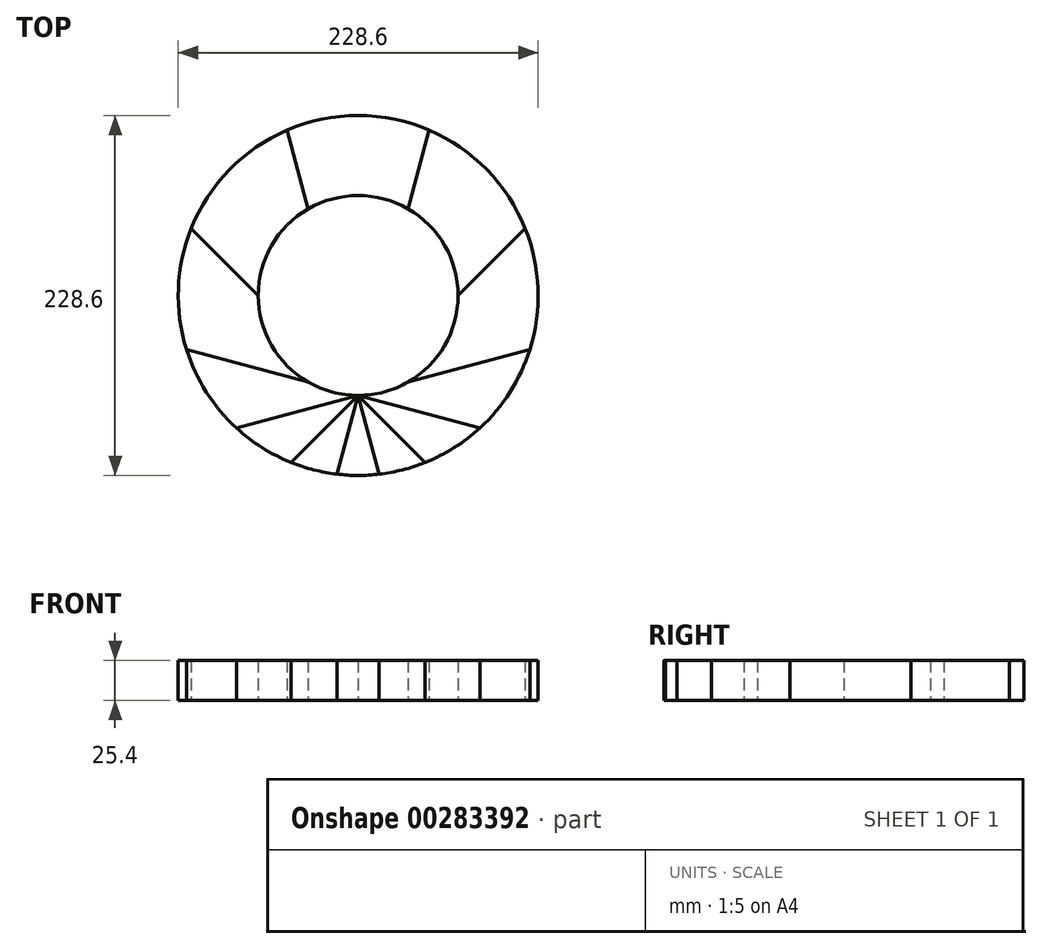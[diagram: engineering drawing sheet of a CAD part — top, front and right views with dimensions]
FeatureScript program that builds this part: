
annotation { "Feature Type Name" : "Feature", "Feature Type Description" : "" }
export const myFeature = defineFeature(function(context is Context, id is Id, definition is map)
    precondition{}
    {
        {
            var Q0;
            Q0=qCreatedBy(makeId("Top.planeOp"),FACE);
            var sketch = newSketch(context, id + "F0", { "sketchPlane" : qUnion([Q0])});
            skCircle(sketch, "E0", {"center": v(0, 0) * mm, "radius": 114.3 * mm});
            skLineSegment(sketch, "E1", {"start": v(0, 0) * mm, "end": v(0, -63.5) * mm, "construction": true});
            skCircle(sketch, "E2", {"center": v(0, 0) * mm, "radius": 63.5 * mm});
            skCircle(sketch, "E3.cCircle", {"center": v(0, -63.5) * mm, "radius": 177.8 * mm, "construction": true});
            skLineSegment(sketch, "E3.0", {"start": v(-47.64, 114.3) * mm, "end": v(47.64, 114.3) * mm, "construction": true});
            skLineSegment(sketch, "E3.1", {"start": v(47.64, 114.3) * mm, "end": v(130.16, 66.66) * mm, "construction": true});
            skLineSegment(sketch, "E3.2", {"start": v(130.16, 66.66) * mm, "end": v(177.8, -15.86) * mm, "construction": true});
            skLineSegment(sketch, "E3.3", {"start": v(177.8, -15.86) * mm, "end": v(177.8, -111.14) * mm, "construction": true});
            skLineSegment(sketch, "E3.4", {"start": v(177.8, -111.14) * mm, "end": v(130.16, -193.66) * mm, "construction": true});
            skLineSegment(sketch, "E3.5", {"start": v(130.16, -193.66) * mm, "end": v(47.64, -241.3) * mm, "construction": true});
            skLineSegment(sketch, "E3.6", {"start": v(47.64, -241.3) * mm, "end": v(-47.64, -241.3) * mm, "construction": true});
            skLineSegment(sketch, "E3.7", {"start": v(-47.64, -241.3) * mm, "end": v(-130.16, -193.66) * mm, "construction": true});
            skLineSegment(sketch, "E3.8", {"start": v(-130.16, -193.66) * mm, "end": v(-177.8, -111.14) * mm, "construction": true});
            skLineSegment(sketch, "E3.9", {"start": v(-177.8, -111.14) * mm, "end": v(-177.8, -15.86) * mm, "construction": true});
            skLineSegment(sketch, "E3.10", {"start": v(-177.8, -15.86) * mm, "end": v(-130.16, 66.66) * mm, "construction": true});
            skLineSegment(sketch, "E3.11", {"start": v(-130.16, 66.66) * mm, "end": v(-47.64, 114.3) * mm, "construction": true});
            skPoint(sketch, "E3.0.midPoint", {"position": v(0, 114.3) * mm});
            skLineSegment(sketch, "E4", {"start": v(0, -63.5) * mm, "end": v(177.8, -111.14) * mm});
            skLineSegment(sketch, "E5.1.0", {"start": v(0, -63.5) * mm, "end": v(177.8, -15.86) * mm});
            skLineSegment(sketch, "E5.2.0", {"start": v(0, -63.5) * mm, "end": v(130.16, 66.66) * mm});
            skLineSegment(sketch, "E5.3.0", {"start": v(0, -63.5) * mm, "end": v(47.64, 114.3) * mm});
            skLineSegment(sketch, "E5.4.0", {"start": v(0, -63.5) * mm, "end": v(-47.64, 114.3) * mm});
            skLineSegment(sketch, "E5.5.0", {"start": v(0, -63.5) * mm, "end": v(-130.16, 66.66) * mm});
            skLineSegment(sketch, "E5.6.0", {"start": v(0, -63.5) * mm, "end": v(-177.8, -15.86) * mm});
            skLineSegment(sketch, "E5.7.0", {"start": v(0, -63.5) * mm, "end": v(-177.8, -111.14) * mm});
            skLineSegment(sketch, "E5.8.0", {"start": v(0, -63.5) * mm, "end": v(-130.16, -193.66) * mm});
            skLineSegment(sketch, "E5.9.0", {"start": v(0, -63.5) * mm, "end": v(-47.64, -241.3) * mm});
            skLineSegment(sketch, "E5.10.0", {"start": v(0, -63.5) * mm, "end": v(47.64, -241.3) * mm});
            skLineSegment(sketch, "E5.11.0", {"start": v(0, -63.5) * mm, "end": v(130.16, -193.66) * mm});
            skSolve(sketch);
        }
        {
            var Q0;
            {var subQ0=sQuery(id+"F0.wireOp",EDGE,"E5.5.0");var subQ1=sQuery(id+"F0.wireOp",EDGE,"E0");var subQ2=makeQuery(id+"F0.imprint","INTERSECT",VERTEX,{"derivedFrom":[subQ1,subQ0]});Q0=makeQuery(id+"F0.imprint","IMPRINT",FACE,{"disambiguationData":[TD([[makeQuery(id+"F0.imprint","IMPRINT",EDGE,{"disambiguationData":[TD([[subQ2,-1.0]])],"derivedFrom":subQ1}),1.0]])]});}
            var Q1;
            {var subQ0=sQuery(id+"F0.wireOp",EDGE,"E5.7.0");var subQ1=sQuery(id+"F0.wireOp",EDGE,"E0");var subQ2=makeQuery(id+"F0.imprint","INTERSECT",VERTEX,{"derivedFrom":[subQ1,subQ0]});Q1=makeQuery(id+"F0.imprint","IMPRINT",FACE,{"disambiguationData":[TD([[makeQuery(id+"F0.imprint","IMPRINT",EDGE,{"disambiguationData":[TD([[subQ2,-1.0]])],"derivedFrom":subQ1}),1.0]])]});}
            var Q2;
            {var subQ0=sQuery(id+"F0.wireOp",EDGE,"E5.9.0");var subQ1=sQuery(id+"F0.wireOp",EDGE,"E0");var subQ2=makeQuery(id+"F0.imprint","INTERSECT",VERTEX,{"derivedFrom":[subQ1,subQ0]});Q2=makeQuery(id+"F0.imprint","IMPRINT",FACE,{"disambiguationData":[TD([[makeQuery(id+"F0.imprint","IMPRINT",EDGE,{"disambiguationData":[TD([[subQ2,-1.0]])],"derivedFrom":subQ1}),1.0]])]});}
            var Q3;
            {var subQ0=sQuery(id+"F0.wireOp",EDGE,"E5.11.0");var subQ1=sQuery(id+"F0.wireOp",EDGE,"E0");var subQ2=makeQuery(id+"F0.imprint","INTERSECT",VERTEX,{"derivedFrom":[subQ1,subQ0]});Q3=makeQuery(id+"F0.imprint","IMPRINT",FACE,{"disambiguationData":[TD([[makeQuery(id+"F0.imprint","IMPRINT",EDGE,{"disambiguationData":[TD([[subQ2,-1.0]])],"derivedFrom":subQ1}),1.0]])]});}
            var Q4;
            {var subQ0=sQuery(id+"F0.wireOp",EDGE,"E5.2.0");var subQ1=sQuery(id+"F0.wireOp",EDGE,"E0");var subQ2=makeQuery(id+"F0.imprint","INTERSECT",VERTEX,{"derivedFrom":[subQ1,subQ0]});Q4=makeQuery(id+"F0.imprint","IMPRINT",FACE,{"disambiguationData":[TD([[makeQuery(id+"F0.imprint","IMPRINT",EDGE,{"disambiguationData":[TD([[subQ2,1.0]])],"derivedFrom":subQ1}),1.0]])]});}
            var Q5;
            {var subQ0=sQuery(id+"F0.wireOp",EDGE,"E5.3.0");var subQ1=sQuery(id+"F0.wireOp",EDGE,"E0");var subQ2=makeQuery(id+"F0.imprint","INTERSECT",VERTEX,{"derivedFrom":[subQ1,subQ0]});Q5=makeQuery(id+"F0.imprint","IMPRINT",FACE,{"disambiguationData":[TD([[makeQuery(id+"F0.imprint","IMPRINT",EDGE,{"disambiguationData":[TD([[subQ2,-1.0]])],"derivedFrom":subQ1}),1.0]])]});}
            extrude(context, id + "F1", {"entities" : qUnion([Q0, Q1, Q2, Q3, Q4, Q5]), "depth" : 25.4 * mm, "offsetDistance" : 25.4 * mm});
        }
        {
            var Q0;
            {var subQ0=sQuery(id+"F0.wireOp",EDGE,"E5.6.0");var subQ1=sQuery(id+"F0.wireOp",EDGE,"E0");var subQ2=makeQuery(id+"F0.imprint","INTERSECT",VERTEX,{"derivedFrom":[subQ1,subQ0]});Q0=makeQuery(id+"F0.imprint","IMPRINT",FACE,{"disambiguationData":[TD([[makeQuery(id+"F0.imprint","IMPRINT",EDGE,{"disambiguationData":[TD([[subQ2,-1.0]])],"derivedFrom":subQ1}),1.0]])]});}
            var Q1;
            {var subQ0=sQuery(id+"F0.wireOp",EDGE,"E5.4.0");var subQ1=sQuery(id+"F0.wireOp",EDGE,"E0");var subQ2=makeQuery(id+"F0.imprint","INTERSECT",VERTEX,{"derivedFrom":[subQ1,subQ0]});Q1=makeQuery(id+"F0.imprint","IMPRINT",FACE,{"disambiguationData":[TD([[makeQuery(id+"F0.imprint","IMPRINT",EDGE,{"disambiguationData":[TD([[subQ2,-1.0]])],"derivedFrom":subQ1}),1.0]])]});}
            var Q2;
            {var subQ0=sQuery(id+"F0.wireOp",EDGE,"E5.3.0");var subQ1=sQuery(id+"F0.wireOp",EDGE,"E0");var subQ2=makeQuery(id+"F0.imprint","INTERSECT",VERTEX,{"derivedFrom":[subQ1,subQ0]});Q2=makeQuery(id+"F0.imprint","IMPRINT",FACE,{"disambiguationData":[TD([[makeQuery(id+"F0.imprint","IMPRINT",EDGE,{"disambiguationData":[TD([[subQ2,1.0]])],"derivedFrom":subQ1}),1.0]])]});}
            var Q3;
            {var subQ0=sQuery(id+"F0.wireOp",EDGE,"E4");var subQ1=sQuery(id+"F0.wireOp",EDGE,"E0");var subQ2=makeQuery(id+"F0.imprint","INTERSECT",VERTEX,{"derivedFrom":[subQ1,subQ0]});Q3=makeQuery(id+"F0.imprint","IMPRINT",FACE,{"disambiguationData":[TD([[makeQuery(id+"F0.imprint","IMPRINT",EDGE,{"disambiguationData":[TD([[subQ2,-1.0]])],"derivedFrom":subQ1}),1.0]])]});}
            var Q4;
            {var subQ0=sQuery(id+"F0.wireOp",EDGE,"E5.10.0");var subQ1=sQuery(id+"F0.wireOp",EDGE,"E0");var subQ2=makeQuery(id+"F0.imprint","INTERSECT",VERTEX,{"derivedFrom":[subQ1,subQ0]});Q4=makeQuery(id+"F0.imprint","IMPRINT",FACE,{"disambiguationData":[TD([[makeQuery(id+"F0.imprint","IMPRINT",EDGE,{"disambiguationData":[TD([[subQ2,-1.0]])],"derivedFrom":subQ1}),1.0]])]});}
            var Q5;
            {var subQ0=sQuery(id+"F0.wireOp",EDGE,"E5.8.0");var subQ1=sQuery(id+"F0.wireOp",EDGE,"E0");var subQ2=makeQuery(id+"F0.imprint","INTERSECT",VERTEX,{"derivedFrom":[subQ1,subQ0]});Q5=makeQuery(id+"F0.imprint","IMPRINT",FACE,{"disambiguationData":[TD([[makeQuery(id+"F0.imprint","IMPRINT",EDGE,{"disambiguationData":[TD([[subQ2,-1.0]])],"derivedFrom":subQ1}),1.0]])]});}
            extrude(context, id + "F2", {"entities" : qUnion([Q0, Q1, Q2, Q3, Q4, Q5]), "depth" : 25.4 * mm, "offsetDistance" : 25.4 * mm});
        }
    });
